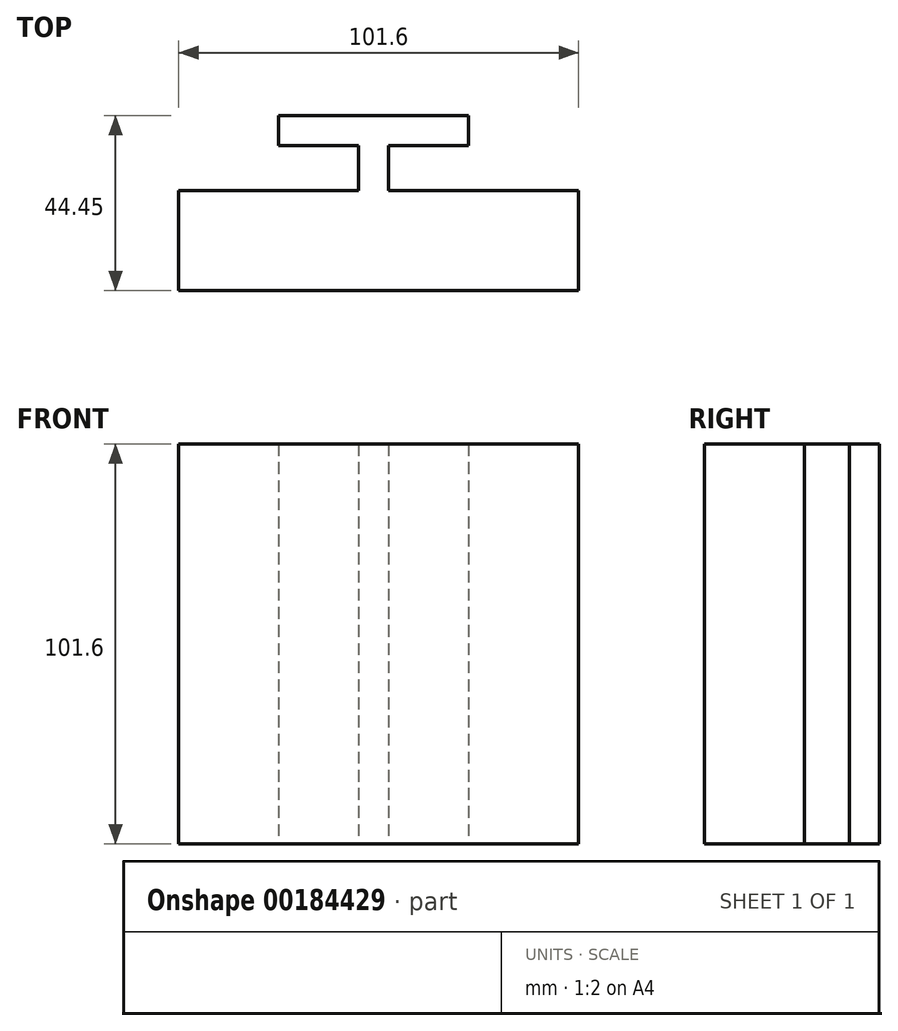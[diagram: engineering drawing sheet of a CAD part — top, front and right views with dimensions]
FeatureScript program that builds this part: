
annotation { "Feature Type Name" : "Feature", "Feature Type Description" : "" }
export const myFeature = defineFeature(function(context is Context, id is Id, definition is map)
    precondition{}
    {
        {
            var Q0;
            Q0=qCreatedBy(makeId("Top.planeOp"),FACE);
            var sketch = newSketch(context, id + "F0", { "sketchPlane" : qUnion([Q0])});
            skLineSegment(sketch, "E0", {"start": v(-0.73, 19.05) * mm, "end": v(47.53, 19.05) * mm});
            skLineSegment(sketch, "E1", {"start": v(47.53, 19.05) * mm, "end": v(47.53, 11.43) * mm});
            skLineSegment(sketch, "E2", {"start": v(47.53, 11.43) * mm, "end": v(27.21, 11.43) * mm});
            skLineSegment(sketch, "E3", {"start": v(27.21, 11.43) * mm, "end": v(27.21, 0) * mm});
            skLineSegment(sketch, "E4", {"start": v(27.21, 0) * mm, "end": v(75.47, 0) * mm});
            skLineSegment(sketch, "E5", {"start": v(75.47, 0) * mm, "end": v(75.47, -25.4) * mm});
            skLineSegment(sketch, "E6", {"start": v(75.47, -25.4) * mm, "end": v(-26.13, -25.4) * mm});
            skLineSegment(sketch, "E7", {"start": v(-26.13, -25.4) * mm, "end": v(-26.13, 0) * mm});
            skLineSegment(sketch, "E8", {"start": v(-26.13, 0) * mm, "end": v(19.6, 0) * mm});
            skLineSegment(sketch, "E9", {"start": v(-0.73, 19.05) * mm, "end": v(-0.73, 11.43) * mm});
            skLineSegment(sketch, "E10", {"start": v(19.6, 11.43) * mm, "end": v(-0.73, 11.43) * mm});
            skLineSegment(sketch, "E11", {"start": v(19.6, 11.43) * mm, "end": v(19.6, 0) * mm});
            skSolve(sketch);
        }
        {
            var Q0;
            Q0=makeQuery(id+"F0.imprint","IMPRINT",FACE,{"disambiguationData":[TD([[makeQuery(id+"F0.imprint","IMPRINT",EDGE,{"derivedFrom":sQuery(id+"F0.wireOp",EDGE,"E0")}),-1.0]])]});
            extrude(context, id + "F1", {"entities" : qUnion([Q0]), "depth" : 101.6 * mm});
        }
    });
